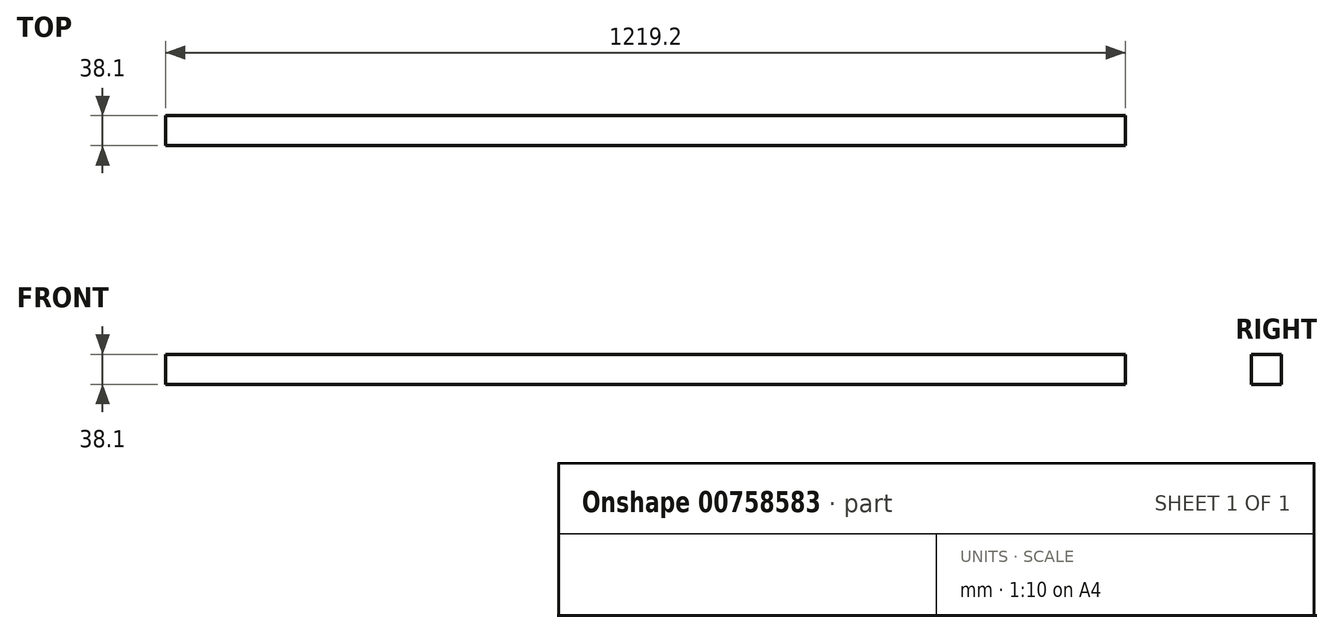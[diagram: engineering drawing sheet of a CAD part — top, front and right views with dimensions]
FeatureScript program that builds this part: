
annotation { "Feature Type Name" : "Feature", "Feature Type Description" : "" }
export const myFeature = defineFeature(function(context is Context, id is Id, definition is map)
    precondition{}
    {
        {
            var Q0;
            Q0=qCreatedBy(makeId("Front.planeOp"),FACE);
            var sketch = newSketch(context, id + "F0", { "sketchPlane" : qUnion([Q0])});
            skLineSegment(sketch, "E0.bottom", {"start": v(-609.6, 19.05) * mm, "end": v(609.6, 19.05) * mm});
            skLineSegment(sketch, "E0.top", {"start": v(-609.6, -19.05) * mm, "end": v(609.6, -19.05) * mm});
            skLineSegment(sketch, "E0.left", {"start": v(-609.6, 19.05) * mm, "end": v(-609.6, -19.05) * mm});
            skLineSegment(sketch, "E0.right", {"start": v(609.6, 19.05) * mm, "end": v(609.6, -19.05) * mm});
            skPoint(sketch, "E0.middle", {"position": v(0, 0) * mm});
            skSolve(sketch);
        }
        {
            var Q0;
            Q0=makeQuery(id+"F0.imprint","IMPRINT",FACE,{"disambiguationData":[TD([[makeQuery(id+"F0.imprint","IMPRINT",EDGE,{"derivedFrom":sQuery(id+"F0.wireOp",EDGE,"E0.bottom")}),-1.0]])]});
            extrude(context, id + "F1", {"entities" : qUnion([Q0]), "endBound" : BoundingType.SYMMETRIC, "depth" : 38.1 * mm, "offsetDistance" : 25.4 * mm});
        }
    });
